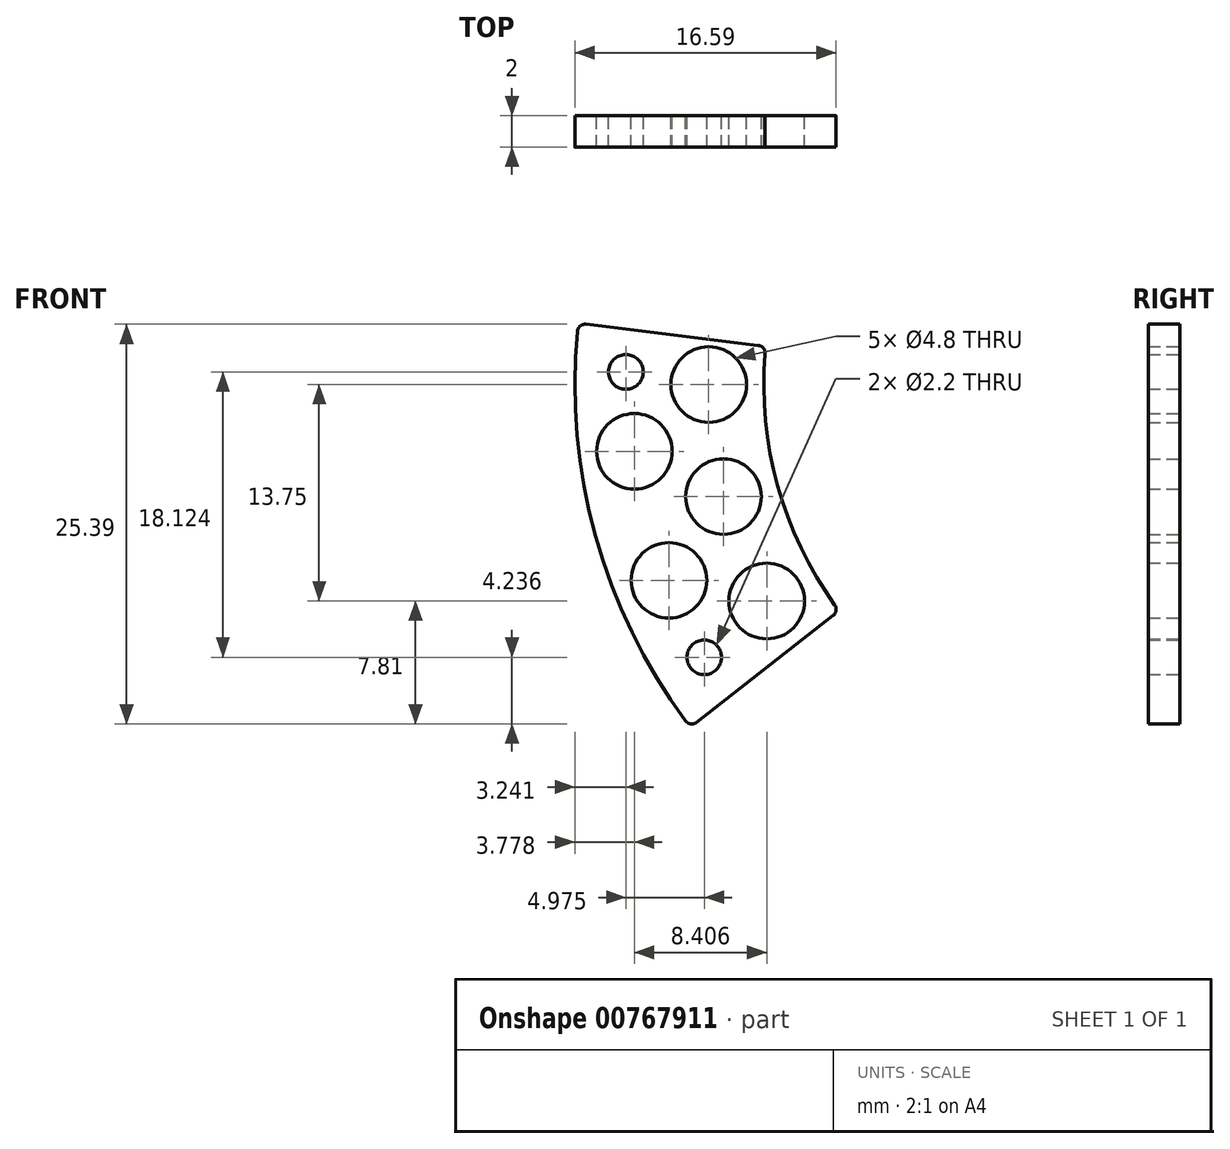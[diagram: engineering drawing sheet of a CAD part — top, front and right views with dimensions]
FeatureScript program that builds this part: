
annotation { "Feature Type Name" : "Feature", "Feature Type Description" : "" }
export const myFeature = defineFeature(function(context is Context, id is Id, definition is map)
    precondition{}
    {
        {
            var Q0;
            Q0=qCreatedBy(makeId("Front.planeOp"),FACE);
            var sketch = newSketch(context, id + "F0", { "sketchPlane" : qUnion([Q0])});
            skArc(sketch, "E0.0", {"start": v(-23.92, 1.95) * mm, "mid": v(-24.03, 2.3) * mm, "end": v(-24.36, 2.49) * mm});
            skArc(sketch, "E0.1", {"start": v(-23.92, 1.95) * mm, "mid": v(-23.13, -6.41) * mm, "end": v(-19.5, -14) * mm});
            skLineSegment(sketch, "E0.2", {"start": v(-24.36, 2.49) * mm, "end": v(-35.28, 3.83) * mm});
            skArc(sketch, "E0.3", {"start": v(-19.6, -14.68) * mm, "mid": v(-19.41, -14.35) * mm, "end": v(-19.5, -14) * mm});
            skArc(sketch, "E0.4", {"start": v(-35.28, 3.83) * mm, "mid": v(-35.66, 3.72) * mm, "end": v(-35.84, 3.38) * mm});
            skArc(sketch, "E0.5", {"start": v(-35.84, 3.38) * mm, "mid": v(-34.7, -9.62) * mm, "end": v(-28.98, -21.36) * mm});
            skArc(sketch, "E0.6", {"start": v(-28.98, -21.36) * mm, "mid": v(-28.65, -21.55) * mm, "end": v(-28.27, -21.45) * mm});
            skLineSegment(sketch, "E0.7", {"start": v(-19.6, -14.68) * mm, "end": v(-28.27, -21.45) * mm});
            skArc(sketch, "E1.MirrorCS", {"start": v(20.88, 11.83) * mm, "mid": v(21.28, 11.1) * mm, "end": v(21.65, 10.36) * mm});
            skFitSpline(sketch, "E2.MirrorCS", {"points": [v(33.34, 13.58) * mm, v(20.88, 11.83) * mm], "startDerivative": vector(-7.87, 19.2) * mm, "endDerivative": vector(10.77, -23.32) * mm});
            skArc(sketch, "E3.MirrorCS", {"start": v(33.34, 13.58) * mm, "mid": v(33.62, 12.88) * mm, "end": v(33.88, 12.18) * mm});
            skFitSpline(sketch, "E4.MirrorCS", {"points": [v(33.34, -13.58) * mm, v(20.88, -11.83) * mm], "startDerivative": vector(-7.87, -19.2) * mm, "endDerivative": vector(10.77, 23.32) * mm});
            skArc(sketch, "E5.MirrorCS", {"start": v(21.65, -10.36) * mm, "mid": v(21.28, -11.1) * mm, "end": v(20.88, -11.83) * mm});
            skCircle(sketch, "E6.MirrorC", {"center": v(23.82, -13.75) * mm, "radius": 2.4 * mm});
            skCircle(sketch, "E7.MirrorC", {"center": v(30.03, -12.44) * mm, "radius": 2.4 * mm});
            skCircle(sketch, "E8.MirrorC", {"center": v(26.56, -7.12) * mm, "radius": 2.4 * mm});
            skCircle(sketch, "E9.MirrorC", {"center": v(32.22, -4.24) * mm, "radius": 2.4 * mm});
            skCircle(sketch, "E10.MirrorC", {"center": v(27.5, 0) * mm, "radius": 2.4 * mm});
            skCircle(sketch, "E11.MirrorC", {"center": v(32.22, 4.24) * mm, "radius": 2.4 * mm});
            skCircle(sketch, "E12.MirrorC", {"center": v(26.56, 7.12) * mm, "radius": 2.4 * mm});
            skCircle(sketch, "E13.MirrorC", {"center": v(30.03, 12.44) * mm, "radius": 2.4 * mm});
            skCircle(sketch, "E14.MirrorC", {"center": v(23.82, 13.75) * mm, "radius": 2.4 * mm});
            skArc(sketch, "E15", {"start": v(21.65, -10.36) * mm, "mid": v(24, 0) * mm, "end": v(21.65, 10.36) * mm});
            skCircle(sketch, "E16", {"center": v(34.77, -9.32) * mm, "radius": 1.1 * mm});
            skArc(sketch, "E17", {"start": v(33.88, -12.18) * mm, "mid": v(37.67, -10.1) * mm, "end": v(35.43, -6.39) * mm});
            skArc(sketch, "E18.trimOffspring", {"start": v(33.88, -12.18) * mm, "mid": v(33.62, -12.88) * mm, "end": v(33.34, -13.58) * mm});
            skCircle(sketch, "E19.MirrorC", {"center": v(34.77, 9.32) * mm, "radius": 1.1 * mm});
            skArc(sketch, "E20.MirrorCS", {"start": v(33.88, 12.18) * mm, "mid": v(37.67, 10.1) * mm, "end": v(35.43, 6.39) * mm});
            skArc(sketch, "E21.trimOffspring", {"start": v(35.43, 6.39) * mm, "mid": v(36, 0) * mm, "end": v(35.43, -6.39) * mm});
            skLineSegment(sketch, "E22", {"start": v(0, 0) * mm, "end": v(0, -36.06) * mm, "construction": true});
            skCircle(sketch, "E23.MirrorC", {"center": v(-23.82, -13.75) * mm, "radius": 2.4 * mm});
            skCircle(sketch, "E24.MirrorC", {"center": v(-30.03, -12.44) * mm, "radius": 2.4 * mm});
            skCircle(sketch, "E25.MirrorC", {"center": v(-26.56, -7.12) * mm, "radius": 2.4 * mm});
            skCircle(sketch, "E26.MirrorC", {"center": v(-32.22, -4.24) * mm, "radius": 2.4 * mm});
            skCircle(sketch, "E27.MirrorC", {"center": v(-27.5, 0) * mm, "radius": 2.4 * mm});
            skLineSegment(sketch, "E28", {"start": v(-23.82, -13.75) * mm, "end": v(-30.03, -12.44) * mm, "construction": true});
            skLineSegment(sketch, "E29", {"start": v(-26.92, -13.1) * mm, "end": v(-28.65, -21.55) * mm, "construction": true});
            skCircle(sketch, "E30", {"center": v(-27.78, -17.32) * mm, "radius": 1.1 * mm});
            skLineSegment(sketch, "E31", {"start": v(-32.22, -4.24) * mm, "end": v(-27.5, 0) * mm, "construction": true});
            skLineSegment(sketch, "E32", {"start": v(-29.86, -2.12) * mm, "end": v(-35.66, 3.72) * mm, "construction": true});
            skCircle(sketch, "E33", {"center": v(-32.76, 0.8) * mm, "radius": 1.1 * mm});
            skSolve(sketch);
        }
        {
            var Q0;
            Q0=makeQuery(id+"F0.imprint","IMPRINT",FACE,{"disambiguationData":[TD([[makeQuery(id+"F0.imprint","IMPRINT",EDGE,{"derivedFrom":sQuery(id+"F0.wireOp",EDGE,"E0.0")}),1.0]])]});
            extrude(context, id + "F1", {"entities" : qUnion([Q0]), "depth" : 2 * mm, "offsetDistance" : 25 * mm});
        }
    });
